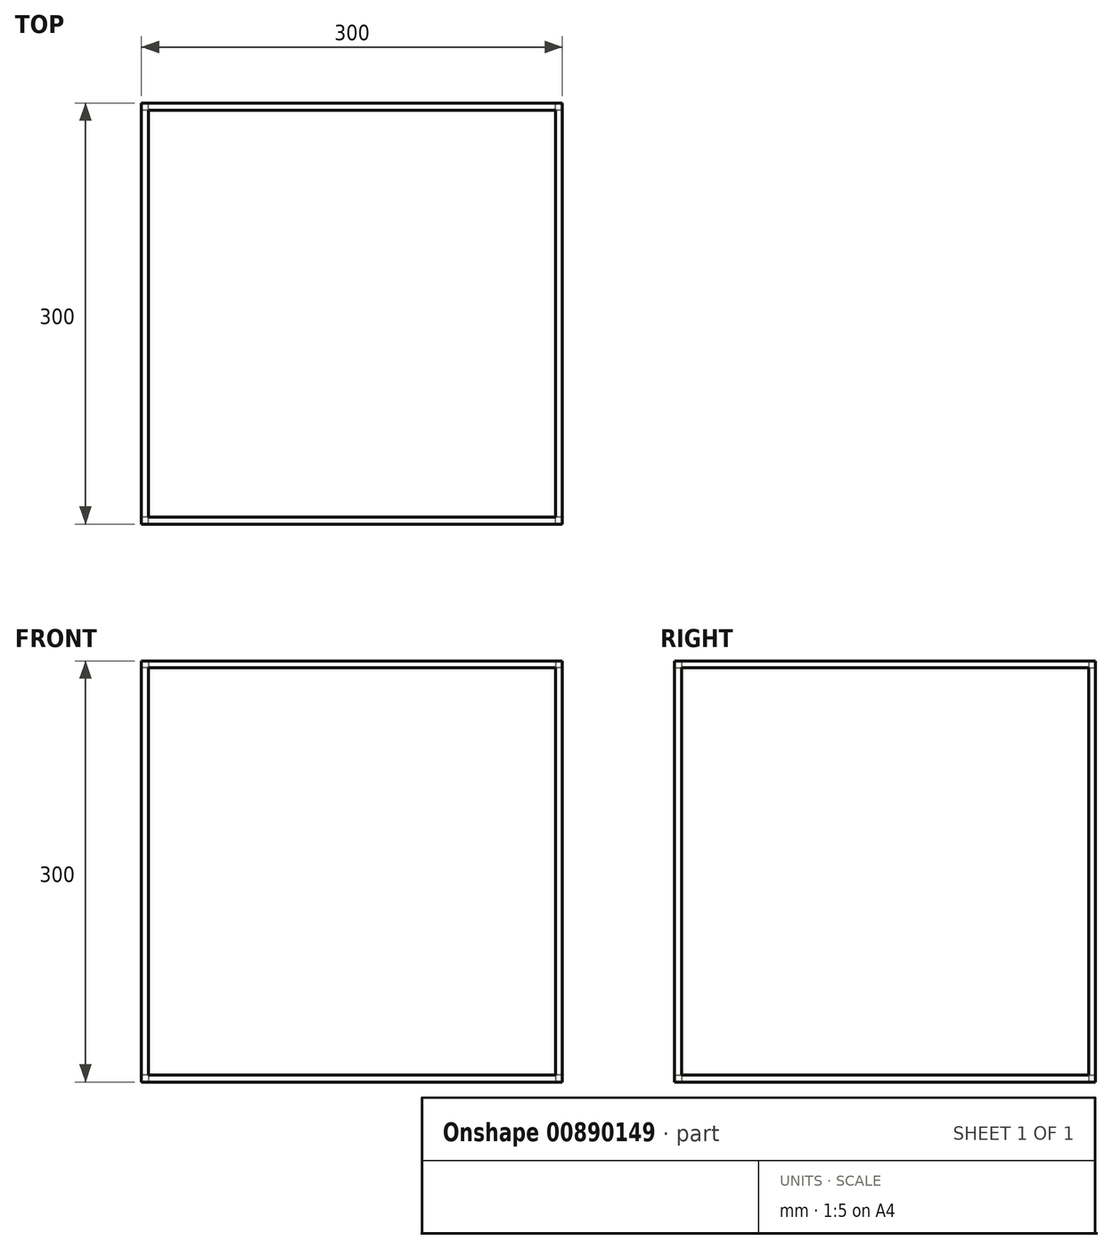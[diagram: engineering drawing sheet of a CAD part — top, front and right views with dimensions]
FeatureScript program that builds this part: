
annotation { "Feature Type Name" : "Feature", "Feature Type Description" : "" }
export const myFeature = defineFeature(function(context is Context, id is Id, definition is map)
    precondition{}
    {
        {
            var Q0;
            Q0=qCreatedBy(makeId("Top.planeOp"),FACE);
            var sketch = newSketch(context, id + "F0", { "sketchPlane" : qUnion([Q0])});
            skLineSegment(sketch, "E0.bottom", {"start": v(-150, 150) * mm, "end": v(150, 150) * mm});
            skLineSegment(sketch, "E0.top", {"start": v(-150, -150) * mm, "end": v(150, -150) * mm});
            skLineSegment(sketch, "E0.left", {"start": v(-150, 150) * mm, "end": v(-150, -150) * mm});
            skLineSegment(sketch, "E0.right", {"start": v(150, 150) * mm, "end": v(150, -150) * mm});
            skPoint(sketch, "E0.middle", {"position": v(0, 0) * mm});
            skLineSegment(sketch, "E1.bottom", {"start": v(-145, 145) * mm, "end": v(145, 145) * mm});
            skLineSegment(sketch, "E1.top", {"start": v(-145, -145) * mm, "end": v(145, -145) * mm});
            skLineSegment(sketch, "E1.left", {"start": v(-145, 145) * mm, "end": v(-145, -145) * mm});
            skLineSegment(sketch, "E1.right", {"start": v(145, 145) * mm, "end": v(145, -145) * mm});
            skSolve(sketch);
        }
        {
            var Q0;
            Q0=qSketchRegion(id+"F0",true);
            extrude(context, id + "F1", {"entities" : qUnion([Q0]), "depth" : 300 * mm});
        }
        {
            var Q0;
            Q0=qCreatedBy(makeId("Front.planeOp"),FACE);
            var sketch = newSketch(context, id + "F2", { "sketchPlane" : qUnion([Q0])});
            skLineSegment(sketch, "E2.bottom", {"start": v(145, 295) * mm, "end": v(-145, 295) * mm});
            skLineSegment(sketch, "E2.top", {"start": v(145, 5) * mm, "end": v(-145, 5) * mm});
            skLineSegment(sketch, "E2.left", {"start": v(145, 295) * mm, "end": v(145, 5) * mm});
            skLineSegment(sketch, "E2.right", {"start": v(-145, 295) * mm, "end": v(-145, 5) * mm});
            skSolve(sketch);
        }
        {
            var Q0;
            Q0=qSketchRegion(id+"F2",true);
            extrude(context, id + "F3", {"entities" : qUnion([Q0]), "operationType" : NewBodyOperationType.REMOVE, "depth" : 300 * mm, "offsetDistance" : 25 * mm, "symmetric" : true});
        }
        {
            var Q0;
            Q0=qCreatedBy(makeId("Right.planeOp"),FACE);
            var sketch = newSketch(context, id + "F4", { "sketchPlane" : qUnion([Q0])});
            skLineSegment(sketch, "E3.bottom", {"start": v(-145, 295) * mm, "end": v(145, 295) * mm});
            skLineSegment(sketch, "E3.top", {"start": v(-145, 5) * mm, "end": v(145, 5) * mm});
            skLineSegment(sketch, "E3.left", {"start": v(-145, 295) * mm, "end": v(-145, 5) * mm});
            skLineSegment(sketch, "E3.right", {"start": v(145, 295) * mm, "end": v(145, 5) * mm});
            skSolve(sketch);
        }
        {
            var Q0;
            Q0=qSketchRegion(id+"F4",true);
            extrude(context, id + "F5", {"entities" : qUnion([Q0]), "operationType" : NewBodyOperationType.REMOVE, "depth" : 300 * mm, "offsetDistance" : 25 * mm, "symmetric" : true});
        }
    });
